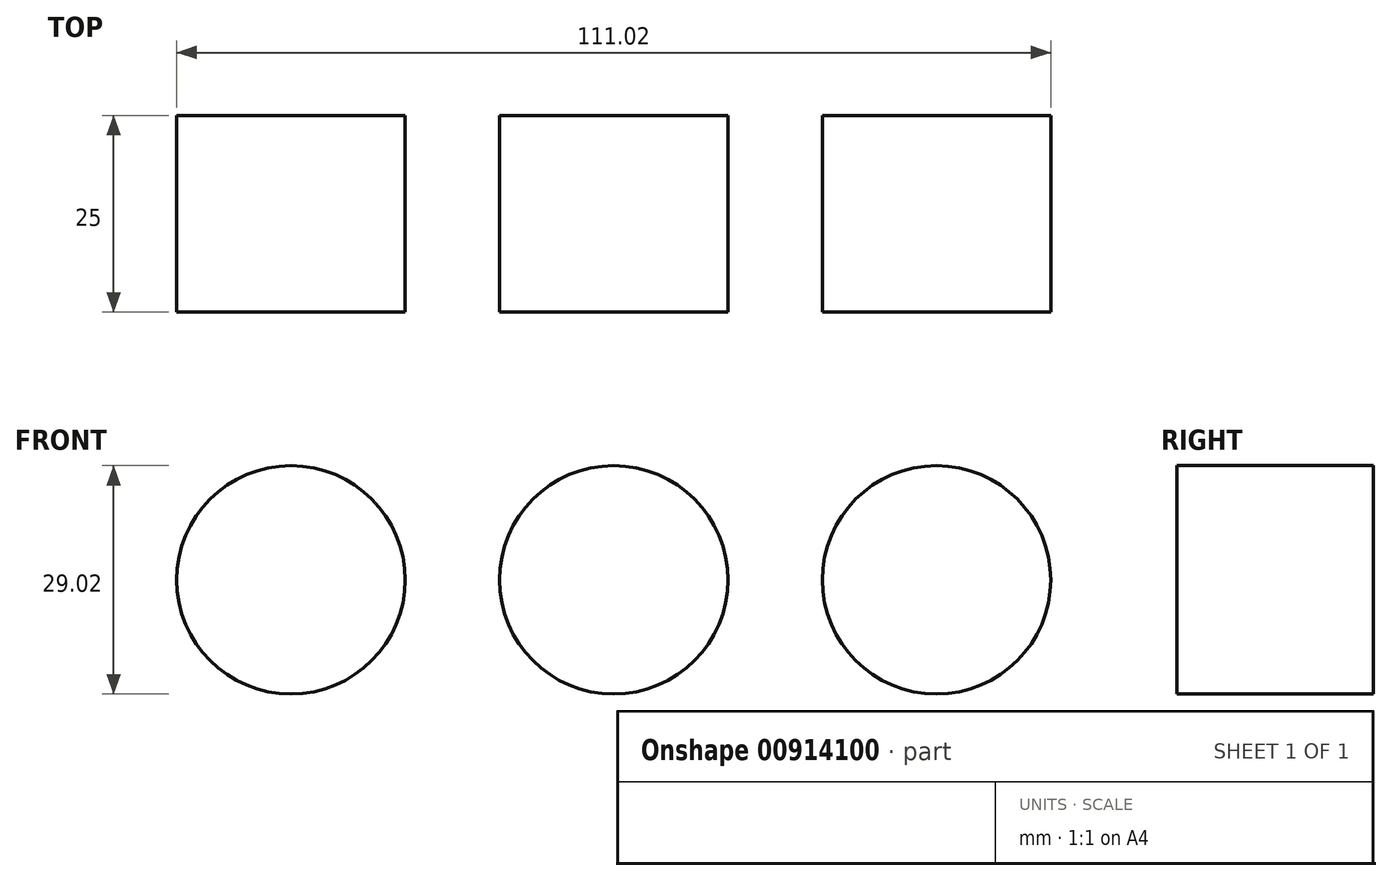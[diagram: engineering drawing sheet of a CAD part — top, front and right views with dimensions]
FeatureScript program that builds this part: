
annotation { "Feature Type Name" : "Feature", "Feature Type Description" : "" }
export const myFeature = defineFeature(function(context is Context, id is Id, definition is map)
    precondition{}
    {
        {
            var Q0;
            Q0=qCreatedBy(makeId("Front.planeOp"),FACE);
            var sketch = newSketch(context, id + "F0", { "sketchPlane" : qUnion([Q0])});
            skCircle(sketch, "E0", {"center": v(0, 0) * mm, "radius": 14.51 * mm});
            skCircle(sketch, "E1.1.0.0", {"center": v(41, 0) * mm, "radius": 14.51 * mm});
            skCircle(sketch, "E1.2.0.0", {"center": v(82, 0) * mm, "radius": 14.51 * mm});
            skLineSegment(sketch, "E1.direction1", {"start": v(0, 0) * mm, "end": v(41, 0) * mm, "construction": true});
            skSolve(sketch);
        }
        {
            var Q0;
            Q0 = qConstructionFilter(qBodyType(qCreatedBy(id + "F0" ,EDGE), BodyType.WIRE), ConstructionObject.NO);
            extrude(context, id + "F1", {"bodyType" : ToolBodyType.SURFACE, "surfaceEntities" : qUnion([Q0]), "depth" : 25 * mm, "offsetDistance" : 25 * mm});
        }
    });
